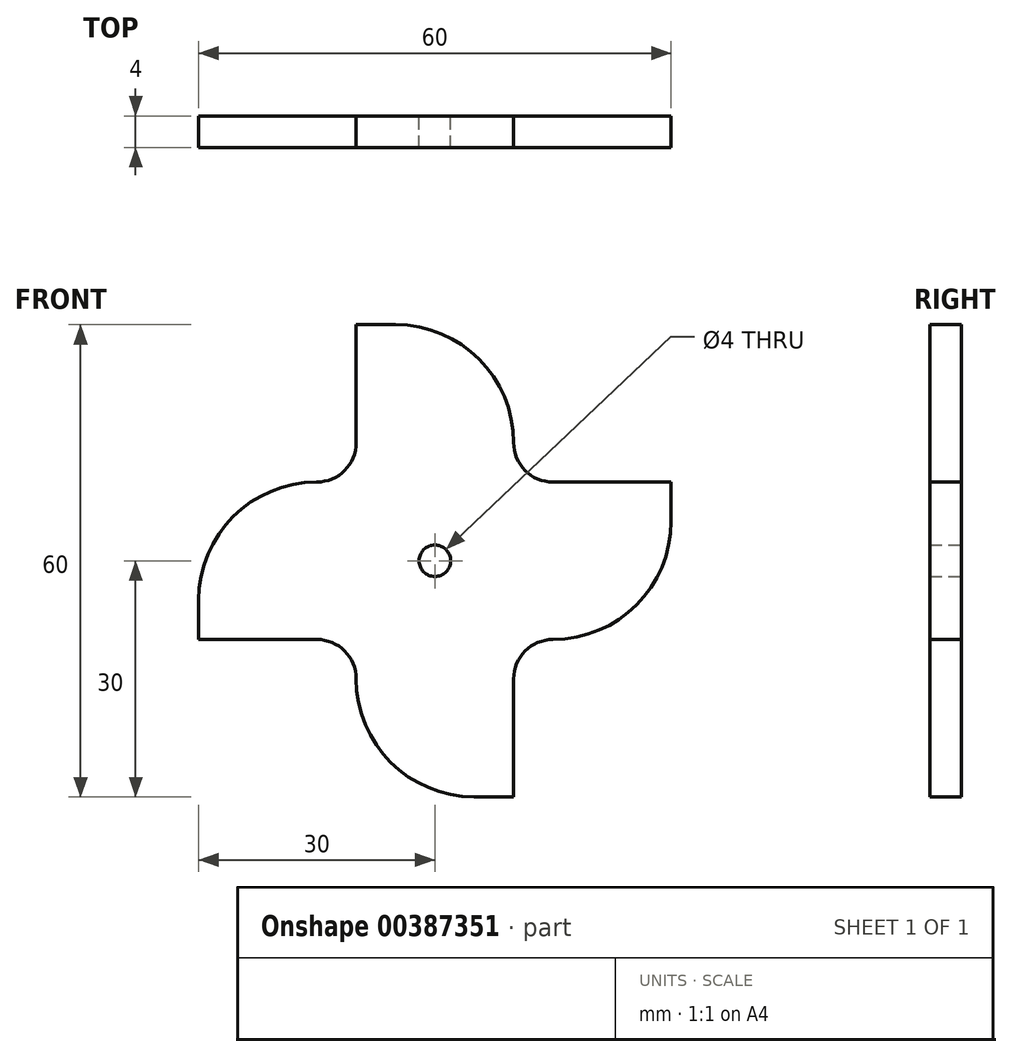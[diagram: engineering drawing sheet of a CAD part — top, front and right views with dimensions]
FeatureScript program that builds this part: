
annotation { "Feature Type Name" : "Feature", "Feature Type Description" : "" }
export const myFeature = defineFeature(function(context is Context, id is Id, definition is map)
    precondition{}
    {
        {
            var Q0;
            Q0=qCreatedBy(makeId("Front.planeOp"),FACE);
            var sketch = newSketch(context, id + "F0", { "sketchPlane" : qUnion([Q0])});
            skPoint(sketch, "E0.middle", {"position": v(0, 0) * mm});
            skLineSegment(sketch, "E1", {"start": v(-10, 12) * mm, "end": v(-10, 15) * mm});
            skLineSegment(sketch, "E2", {"start": v(5, 30) * mm, "end": v(10, 30) * mm});
            skLineSegment(sketch, "E3", {"start": v(10, 30) * mm, "end": v(10, 12) * mm});
            skLineSegment(sketch, "E4", {"start": v(12, 10) * mm, "end": v(15, 10) * mm});
            skLineSegment(sketch, "E5", {"start": v(30, -10) * mm, "end": v(30, -5) * mm});
            skLineSegment(sketch, "E6", {"start": v(12, -10) * mm, "end": v(30, -10) * mm});
            skLineSegment(sketch, "E7", {"start": v(10, -12) * mm, "end": v(10, -15) * mm});
            skLineSegment(sketch, "E8", {"start": v(-5, -30) * mm, "end": v(-10, -30) * mm});
            skLineSegment(sketch, "E9", {"start": v(-10, -30) * mm, "end": v(-10, -12) * mm});
            skLineSegment(sketch, "E10", {"start": v(-12, -10) * mm, "end": v(-15, -10) * mm});
            skLineSegment(sketch, "E11", {"start": v(-30, 5) * mm, "end": v(-30, 10) * mm});
            skLineSegment(sketch, "E12", {"start": v(-30, 10) * mm, "end": v(-12, 10) * mm});
            skPoint(sketch, "E13.visualSharp", {"position": v(-10, 30) * mm});
            skArc(sketch, "E13.filletArc", {"start": v(5, 30) * mm, "mid": v(-5.6, 25.6) * mm, "end": v(-10, 15) * mm});
            skPoint(sketch, "E14.visualSharp", {"position": v(-30, -10) * mm});
            skArc(sketch, "E14.filletArc", {"start": v(-30, 5) * mm, "mid": v(-25.6, -5.6) * mm, "end": v(-15, -10) * mm});
            skPoint(sketch, "E15.visualSharp", {"position": v(10, -30) * mm});
            skArc(sketch, "E15.filletArc", {"start": v(-5, -30) * mm, "mid": v(5.6, -25.6) * mm, "end": v(10, -15) * mm});
            skPoint(sketch, "E16.visualSharp", {"position": v(30, 10) * mm});
            skArc(sketch, "E16.filletArc", {"start": v(30, -5) * mm, "mid": v(25.6, 5.6) * mm, "end": v(15, 10) * mm});
            skCircle(sketch, "E17", {"center": v(0, 0) * mm, "radius": 2 * mm});
            skPoint(sketch, "E18.visualSharp", {"position": v(10, 10) * mm});
            skArc(sketch, "E18.filletArc", {"start": v(10, 12) * mm, "mid": v(10.59, 10.59) * mm, "end": v(12, 10) * mm});
            skPoint(sketch, "E19.visualSharp", {"position": v(10, -10) * mm});
            skArc(sketch, "E19.filletArc", {"start": v(12, -10) * mm, "mid": v(10.59, -10.59) * mm, "end": v(10, -12) * mm});
            skPoint(sketch, "E20.visualSharp", {"position": v(-10, 10) * mm});
            skArc(sketch, "E20.filletArc", {"start": v(-12, 10) * mm, "mid": v(-10.59, 10.59) * mm, "end": v(-10, 12) * mm});
            skPoint(sketch, "E21.visualSharp", {"position": v(-10, -10) * mm});
            skArc(sketch, "E21.filletArc", {"start": v(-10, -12) * mm, "mid": v(-10.59, -10.59) * mm, "end": v(-12, -10) * mm});
            skSolve(sketch);
        }
        {
            var Q0;
            Q0=qCreatedBy(makeId("Front.planeOp"),FACE);
            var sketch = newSketch(context, id + "F1", { "sketchPlane" : qUnion([Q0])});
            skPoint(sketch, "E22.middle", {"position": v(0, 0) * mm});
            skLineSegment(sketch, "E23", {"start": v(10, 15) * mm, "end": v(10, 15) * mm});
            skLineSegment(sketch, "E24", {"start": v(-5, 30) * mm, "end": v(-10, 30) * mm});
            skLineSegment(sketch, "E25", {"start": v(-10, 30) * mm, "end": v(-10, 15) * mm});
            skLineSegment(sketch, "E26", {"start": v(-15, 10) * mm, "end": v(-15, 10) * mm});
            skLineSegment(sketch, "E27", {"start": v(-30, -5) * mm, "end": v(-30, -10) * mm});
            skLineSegment(sketch, "E28", {"start": v(-30, -10) * mm, "end": v(-15, -10) * mm});
            skLineSegment(sketch, "E29", {"start": v(-10, -15) * mm, "end": v(-10, -15) * mm});
            skLineSegment(sketch, "E30", {"start": v(5, -30) * mm, "end": v(10, -30) * mm});
            skLineSegment(sketch, "E31", {"start": v(10, -30) * mm, "end": v(10, -15) * mm});
            skLineSegment(sketch, "E32", {"start": v(15, -10) * mm, "end": v(15, -10) * mm});
            skLineSegment(sketch, "E33", {"start": v(30, 5) * mm, "end": v(30, 10) * mm});
            skLineSegment(sketch, "E34", {"start": v(30, 10) * mm, "end": v(15, 10) * mm});
            skPoint(sketch, "E35.visualSharp", {"position": v(10, 30) * mm});
            skArc(sketch, "E35.filletArc", {"start": v(10, 15) * mm, "mid": v(5.6, 25.6) * mm, "end": v(-5, 30) * mm});
            skPoint(sketch, "E36.visualSharp", {"position": v(30, -10) * mm});
            skArc(sketch, "E36.filletArc", {"start": v(15, -10) * mm, "mid": v(25.6, -5.6) * mm, "end": v(30, 5) * mm});
            skPoint(sketch, "E37.visualSharp", {"position": v(-10, -30) * mm});
            skArc(sketch, "E37.filletArc", {"start": v(-10, -15) * mm, "mid": v(-5.6, -25.6) * mm, "end": v(5, -30) * mm});
            skPoint(sketch, "E38.visualSharp", {"position": v(-30, 10) * mm});
            skArc(sketch, "E38.filletArc", {"start": v(-15, 10) * mm, "mid": v(-25.6, 5.6) * mm, "end": v(-30, -5) * mm});
            skPoint(sketch, "E39.visualSharp", {"position": v(-10, 10) * mm});
            skArc(sketch, "E39.filletArc", {"start": v(-15, 10) * mm, "mid": v(-11.46, 11.46) * mm, "end": v(-10, 15) * mm});
            skPoint(sketch, "E40.visualSharp", {"position": v(10, 10) * mm});
            skArc(sketch, "E40.filletArc", {"start": v(10, 15) * mm, "mid": v(11.46, 11.46) * mm, "end": v(15, 10) * mm});
            skPoint(sketch, "E41.visualSharp", {"position": v(10, -10) * mm});
            skArc(sketch, "E41.filletArc", {"start": v(15, -10) * mm, "mid": v(11.46, -11.46) * mm, "end": v(10, -15) * mm});
            skPoint(sketch, "E42.visualSharp", {"position": v(-10, -10) * mm});
            skArc(sketch, "E42.filletArc", {"start": v(-10, -15) * mm, "mid": v(-11.46, -11.46) * mm, "end": v(-15, -10) * mm});
            skCircle(sketch, "E43", {"center": v(0, 0) * mm, "radius": 2 * mm});
            skSolve(sketch);
        }
        {
            var Q0;
            Q0=makeQuery(id+"F1.imprint","IMPRINT",FACE,{"disambiguationData":[TD([[makeQuery(id+"F1.imprint","IMPRINT",EDGE,{"derivedFrom":sQuery(id+"F1.wireOp",EDGE,"E24")}),1.0]])]});
            extrude(context, id + "F2", {"entities" : qUnion([Q0]), "depth" : 4 * mm, "offsetDistance" : 25 * mm});
        }
    });
